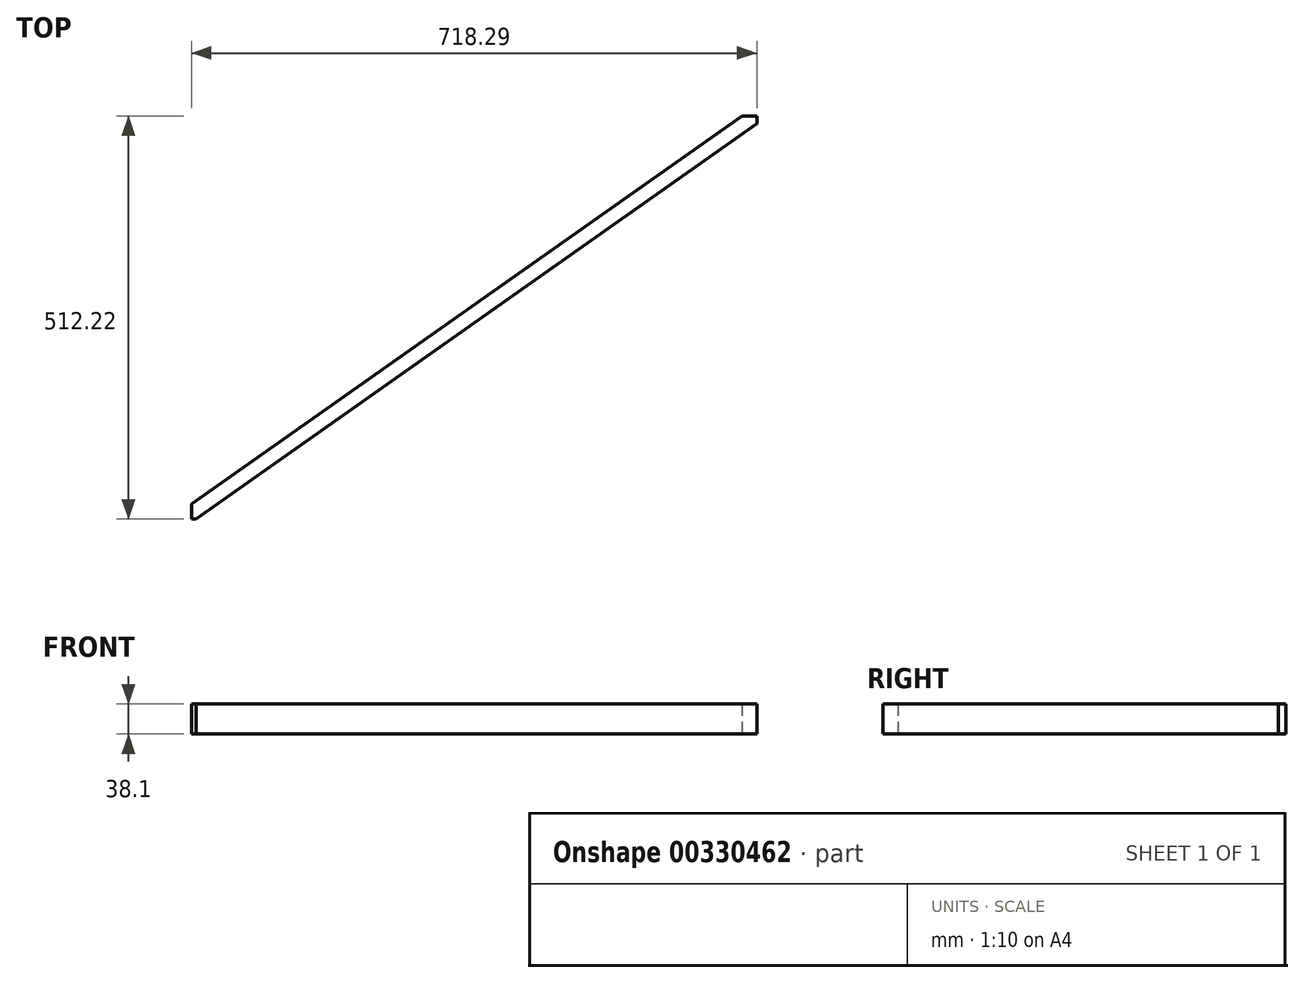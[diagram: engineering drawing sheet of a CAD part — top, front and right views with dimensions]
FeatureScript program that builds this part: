
annotation { "Feature Type Name" : "Feature", "Feature Type Description" : "" }
export const myFeature = defineFeature(function(context is Context, id is Id, definition is map)
    precondition{}
    {
        {
            var Q0;
            Q0=qCreatedBy(makeId("Top.planeOp"),FACE);
            var sketch = newSketch(context, id + "F0", { "sketchPlane" : qUnion([Q0])});
            skLineSegment(sketch, "E0.bottom", {"start": v(0, 0) * mm, "end": v(718.29, 0) * mm, "construction": true});
            skLineSegment(sketch, "E0.top", {"start": v(0, -512.22) * mm, "end": v(718.29, -512.22) * mm, "construction": true});
            skLineSegment(sketch, "E0.left", {"start": v(0, 0) * mm, "end": v(0, -512.22) * mm, "construction": true});
            skLineSegment(sketch, "E0.right", {"start": v(718.29, 0) * mm, "end": v(718.29, -512.22) * mm, "construction": true});
            skLineSegment(sketch, "E1", {"start": v(0, -493.17) * mm, "end": v(0, -512.22) * mm});
            skLineSegment(sketch, "E2", {"start": v(0, -516.48) * mm, "end": v(732.29, 0) * mm});
            skLineSegment(sketch, "E3", {"start": v(732.29, 0) * mm, "end": v(699.24, 0) * mm});
            skLineSegment(sketch, "E4", {"start": v(699.24, 0) * mm, "end": v(0, -493.17) * mm});
            skLineSegment(sketch, "E5", {"start": v(0, -493.17) * mm, "end": v(0, -516.48) * mm});
            skLineSegment(sketch, "E6", {"start": v(0, -512.22) * mm, "end": v(6.04, -512.22) * mm});
            skLineSegment(sketch, "E7", {"start": v(718.29, 0) * mm, "end": v(718.29, -9.88) * mm});
            skSolve(sketch);
        }
        {
            var Q0;
            {var subQ0=sQuery(id+"F0.wireOp",EDGE,"E4");Q0=makeQuery(id+"F0.imprint","IMPRINT",FACE,{"disambiguationData":[TD([[makeQuery(id+"F0.imprint","IMPRINT",EDGE,{"derivedFrom":subQ0}),1.0]])]});}
            extrude(context, id + "F1", {"entities" : qUnion([Q0]), "depth" : 38.1 * mm});
        }
    });
